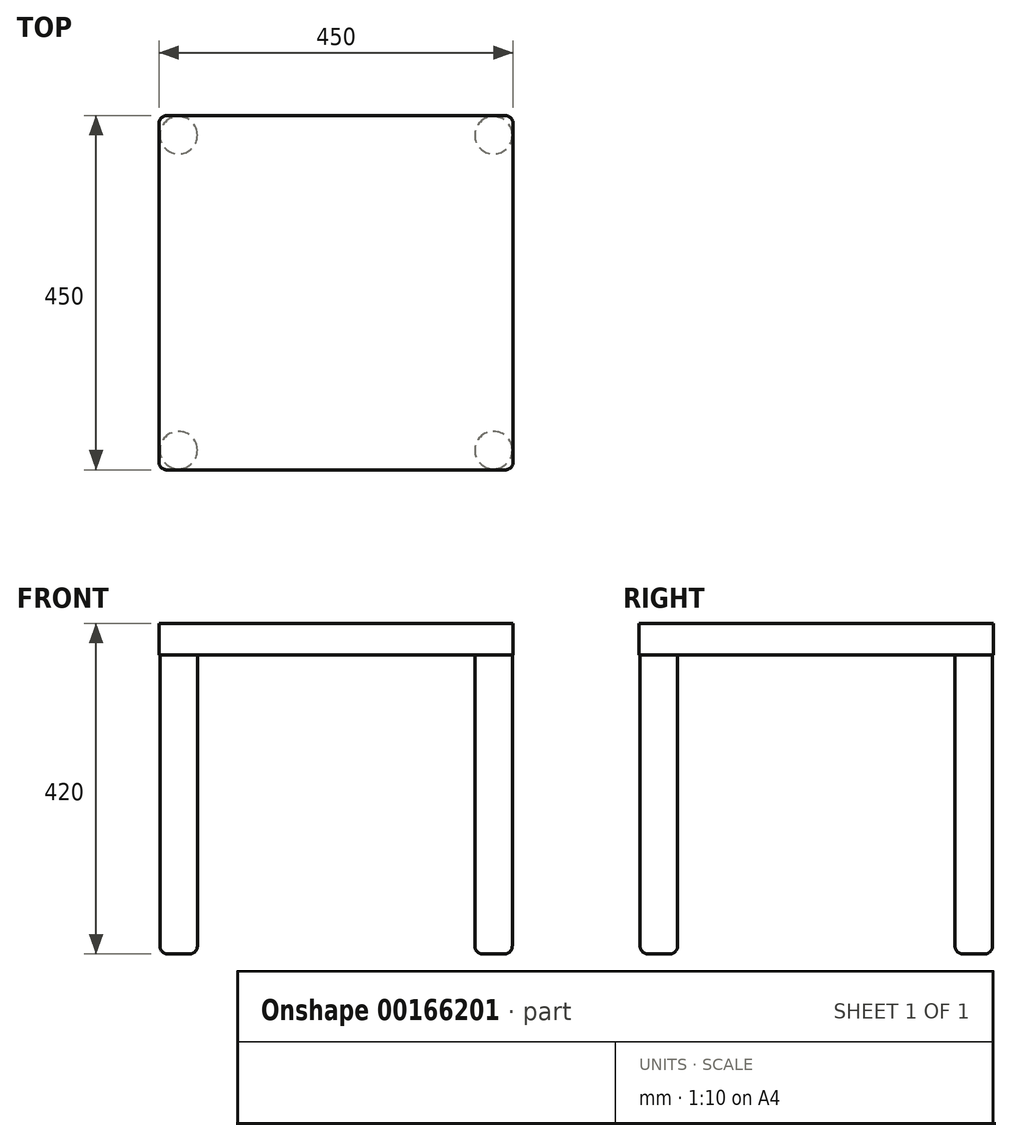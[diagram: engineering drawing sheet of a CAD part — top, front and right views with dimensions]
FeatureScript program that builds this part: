
annotation { "Feature Type Name" : "Feature", "Feature Type Description" : "" }
export const myFeature = defineFeature(function(context is Context, id is Id, definition is map)
    precondition{}
    {
        {
            var Q0;
            Q0=qCreatedBy(makeId("Top.planeOp"),FACE);
            var sketch = newSketch(context, id + "F0", { "sketchPlane" : qUnion([Q0])});
            skLineSegment(sketch, "E0.bottom", {"start": v(-225, 225) * mm, "end": v(225, 225) * mm});
            skLineSegment(sketch, "E0.top", {"start": v(-225, -225) * mm, "end": v(225, -225) * mm});
            skLineSegment(sketch, "E0.left", {"start": v(-225, 225) * mm, "end": v(-225, -225) * mm});
            skLineSegment(sketch, "E0.right", {"start": v(225, 225) * mm, "end": v(225, -225) * mm});
            skPoint(sketch, "E0.middle", {"position": v(0, 0) * mm});
            skCircle(sketch, "E1", {"center": v(-200, 200) * mm, "radius": 23.78 * mm});
            skCircle(sketch, "E2", {"center": v(200, 200) * mm, "radius": 23.78 * mm});
            skCircle(sketch, "E3", {"center": v(200, -200) * mm, "radius": 23.78 * mm});
            skCircle(sketch, "E4", {"center": v(-200, -200) * mm, "radius": 23.78 * mm});
            skSolve(sketch);
        }
        {
            var Q0;
            Q0=makeQuery(id+"F0.imprint","IMPRINT",FACE,{"disambiguationData":[TD([[makeQuery(id+"F0.imprint","IMPRINT",EDGE,{"derivedFrom":sQuery(id+"F0.wireOp",EDGE,"E0.bottom")}),-1.0]])]});
            extrude(context, id + "F1", {"entities" : qUnion([Q0]), "depth" : 40 * mm});
        }
        {
            var Q0;
            Q0=makeQuery(id+"F1.opExtrude","CAP_FACE",FACE,{"disambiguationData":[OSD([sQuery(id+"F0.wireOp",EDGE,"E0.bottom"),sQuery(id+"F0.wireOp",EDGE,"E0.top"),sQuery(id+"F0.wireOp",EDGE,"E0.left"),sQuery(id+"F0.wireOp",EDGE,"E0.right"),sQuery(id+"F0.wireOp",EDGE,"E1"),sQuery(id+"F0.wireOp",EDGE,"E2"),sQuery(id+"F0.wireOp",EDGE,"E3"),sQuery(id+"F0.wireOp",EDGE,"E4")])],"isStart":false});
            var sketch = newSketch(context, id + "F2", { "sketchPlane" : qUnion([Q0])});
            skCircle(sketch, "E5.0", {"center": v(-200, -200) * mm, "radius": 23.78 * mm});
            skCircle(sketch, "E5.1", {"center": v(-200, 200) * mm, "radius": 23.78 * mm});
            skCircle(sketch, "E5.2", {"center": v(200, 200) * mm, "radius": 23.78 * mm});
            skCircle(sketch, "E5.3", {"center": v(200, -200) * mm, "radius": 23.78 * mm});
            skSolve(sketch);
        }
        {
            var Q0;
            Q0 = qSketchRegion(id + "F2", true);
            extrude(context, id + "F3", {"entities" : qUnion([Q0]), "operationType" : NewBodyOperationType.ADD, "oppositeDirection" : true, "depth" : 420 * mm});
        }
        {
            var Q0;
            Q0=makeQuery(id+"F3.opExtrude","CAP_FACE",FACE,{"disambiguationData":[OSD([sQuery(id+"F2.wireOp",EDGE,"E5.0")])],"isStart":false});
            var Q1;
            Q1=makeQuery(id+"F3.opExtrude","CAP_FACE",FACE,{"disambiguationData":[OSD([sQuery(id+"F2.wireOp",EDGE,"E5.3")])],"isStart":false});
            var Q2;
            Q2=makeQuery(id+"F3.opExtrude","CAP_FACE",FACE,{"disambiguationData":[OSD([sQuery(id+"F2.wireOp",EDGE,"E5.2")])],"isStart":false});
            var Q3;
            Q3=makeQuery(id+"F3.opExtrude","CAP_FACE",FACE,{"disambiguationData":[OSD([sQuery(id+"F2.wireOp",EDGE,"E5.1")])],"isStart":false});
            fillet(context, id + "F4", {"entities" : qUnion([Q0, Q1, Q2, Q3]), "radius" : 10 * mm, "tangentPropagation" : true, "allowEdgeOverflow" : false});
        }
        {
            var Q0;
            Q0=makeQuery(id+"F1.opExtrude","SWEPT_EDGE",EDGE,{"disambiguationData":[OSD([sQuery(id+"F0.wireOp",EDGE,"E0.top"),sQuery(id+"F0.wireOp",EDGE,"E0.right")])]});
            var Q1;
            Q1=makeQuery(id+"F1.opExtrude","SWEPT_EDGE",EDGE,{"disambiguationData":[OSD([sQuery(id+"F0.wireOp",EDGE,"E0.bottom"),sQuery(id+"F0.wireOp",EDGE,"E0.right")])]});
            var Q2;
            Q2=makeQuery(id+"F1.opExtrude","SWEPT_EDGE",EDGE,{"disambiguationData":[OSD([sQuery(id+"F0.wireOp",EDGE,"E0.top"),sQuery(id+"F0.wireOp",EDGE,"E0.left")])]});
            var Q3;
            Q3=makeQuery(id+"F1.opExtrude","SWEPT_EDGE",EDGE,{"disambiguationData":[OSD([sQuery(id+"F0.wireOp",EDGE,"E0.bottom"),sQuery(id+"F0.wireOp",EDGE,"E0.left")])]});
            fillet(context, id + "F5", {"entities" : qUnion([Q0, Q1, Q2, Q3]), "radius" : 10 * mm, "tangentPropagation" : true, "allowEdgeOverflow" : false});
        }
    });
